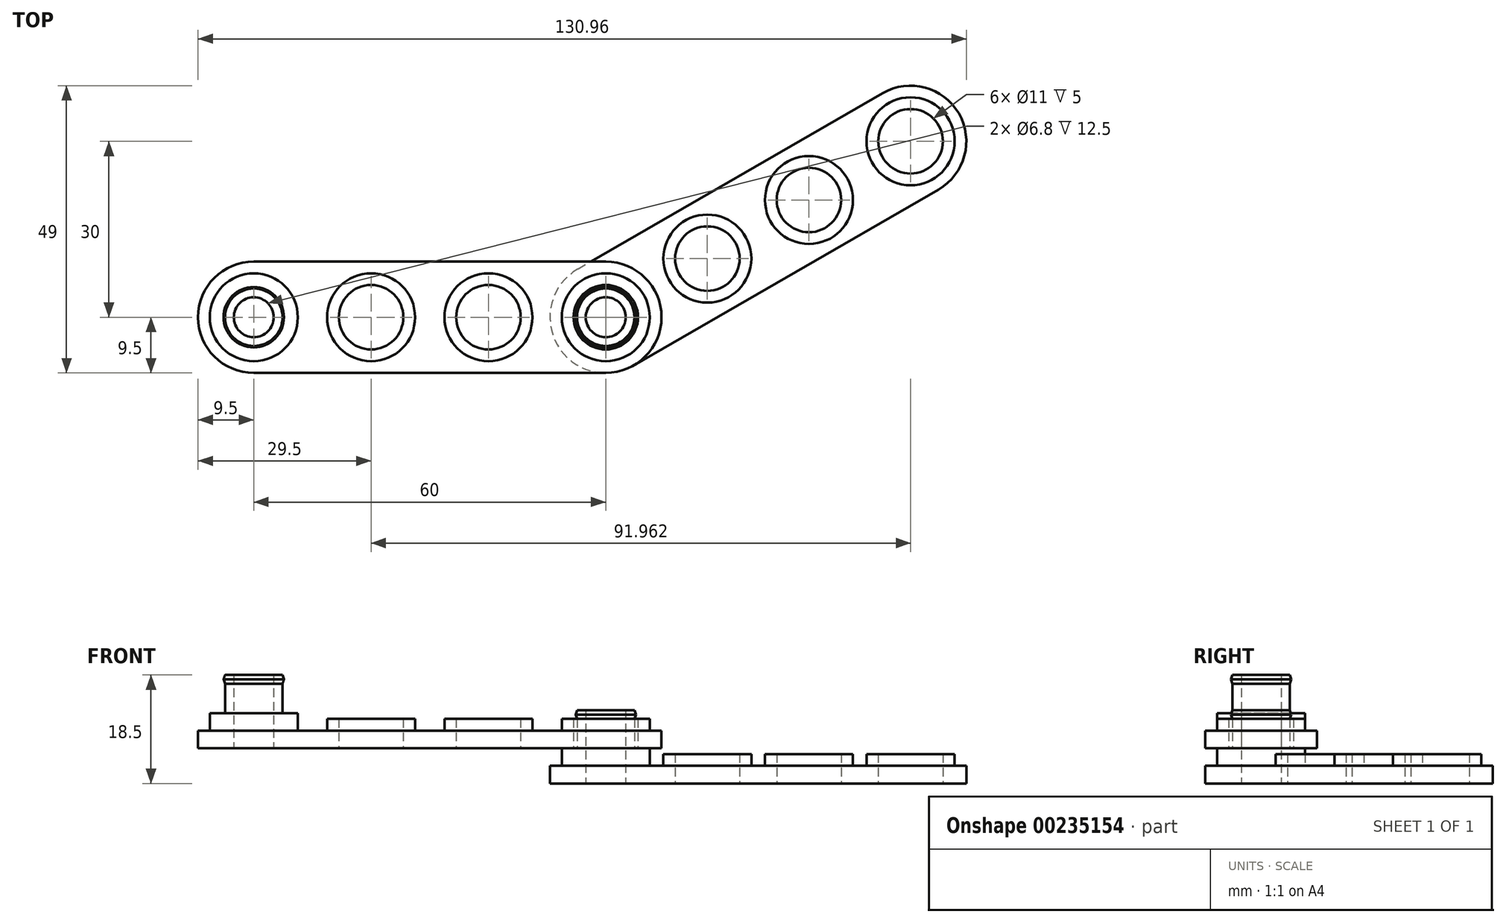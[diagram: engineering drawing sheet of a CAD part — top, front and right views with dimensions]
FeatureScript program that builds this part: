
annotation { "Feature Type Name" : "Feature", "Feature Type Description" : "" }
export const myFeature = defineFeature(function(context is Context, id is Id, definition is map)
    precondition{}
    {
        {
            var Q0;
            Q0=qCreatedBy(makeId("Top.planeOp"),FACE);
            var sketch = newSketch(context, id + "F0", { "sketchPlane" : qUnion([Q0])});
            skCircle(sketch, "E0", {"center": v(0, 0) * mm, "radius": 9.5 * mm});
            skLineSegment(sketch, "E1.bottom", {"start": v(0, 9.5) * mm, "end": v(60, 9.5) * mm});
            skLineSegment(sketch, "E1.top", {"start": v(0, -9.5) * mm, "end": v(60, -9.5) * mm});
            skCircle(sketch, "E2", {"center": v(60, 0) * mm, "radius": 9.5 * mm});
            skCircle(sketch, "E3", {"center": v(20, 0) * mm, "radius": 7.5 * mm});
            skCircle(sketch, "E4", {"center": v(0, 0) * mm, "radius": 7.5 * mm});
            skCircle(sketch, "E5", {"center": v(40, 0) * mm, "radius": 7.5 * mm});
            skCircle(sketch, "E6", {"center": v(60, 0) * mm, "radius": 7.5 * mm});
            skCircle(sketch, "E7", {"center": v(20, 0) * mm, "radius": 5.5 * mm});
            skCircle(sketch, "E8", {"center": v(40, 0) * mm, "radius": 5.5 * mm});
            skCircle(sketch, "E9", {"center": v(60, 0) * mm, "radius": 5.5 * mm});
            skCircle(sketch, "E10", {"center": v(0, 0) * mm, "radius": 4.9 * mm});
            skCircle(sketch, "E11", {"center": v(0, 0) * mm, "radius": 3.4 * mm});
            skSolve(sketch);
        }
        {
            var Q0;
            Q0 = qSketchRegion(id + "F0", true);
            extrude(context, id + "F1", {"entities" : qUnion([Q0]), "depth" : 3 * mm});
        }
        {
            var Q0;
            Q0=makeQuery(id+"F0.imprint","IMPRINT",FACE,{"disambiguationData":[TD([[makeQuery(id+"F0.imprint","IMPRINT",EDGE,{"derivedFrom":sQuery(id+"F0.wireOp",EDGE,"E3")}),1.0]])]});
            var Q1;
            Q1=makeQuery(id+"F0.imprint","IMPRINT",FACE,{"disambiguationData":[TD([[makeQuery(id+"F0.imprint","IMPRINT",EDGE,{"derivedFrom":sQuery(id+"F0.wireOp",EDGE,"E5")}),1.0]])]});
            var Q2;
            Q2=makeQuery(id+"F0.imprint","IMPRINT",FACE,{"disambiguationData":[TD([[makeQuery(id+"F0.imprint","IMPRINT",EDGE,{"derivedFrom":sQuery(id+"F0.wireOp",EDGE,"E6")}),1.0]])]});
            extrude(context, id + "F2", {"entities" : qUnion([Q0, Q1, Q2]), "operationType" : NewBodyOperationType.ADD, "depth" : 5 * mm});
        }
        {
            var Q0;
            Q0=makeQuery(id+"F0.imprint","IMPRINT",FACE,{"disambiguationData":[TD([[makeQuery(id+"F0.imprint","IMPRINT",EDGE,{"derivedFrom":sQuery(id+"F0.wireOp",EDGE,"E4")}),1.0]])]});
            extrude(context, id + "F3", {"entities" : qUnion([Q0]), "operationType" : NewBodyOperationType.ADD, "depth" : 6 * mm});
        }
        {
            var Q0;
            Q0=makeQuery(id+"F0.imprint","IMPRINT",FACE,{"disambiguationData":[TD([[makeQuery(id+"F0.imprint","IMPRINT",EDGE,{"derivedFrom":sQuery(id+"F0.wireOp",EDGE,"E10")}),1.0]])]});
            extrude(context, id + "F4", {"entities" : qUnion([Q0]), "operationType" : NewBodyOperationType.ADD, "depth" : 12.5 * mm});
        }
        {
            var Q0;
            Q0=qCreatedBy(makeId("Front.planeOp"),FACE);
            var sketch = newSketch(context, id + "F5", { "sketchPlane" : qUnion([Q0])});
            skLineSegment(sketch, "E12.bottom", {"start": v(0, 0) * mm, "end": v(4.9, 0) * mm});
            skLineSegment(sketch, "E12.top", {"start": v(0, 12.5) * mm, "end": v(4.9, 12.5) * mm});
            skLineSegment(sketch, "E12.left", {"start": v(0, 0) * mm, "end": v(0, 12.5) * mm});
            skLineSegment(sketch, "E12.right", {"start": v(4.9, 0) * mm, "end": v(4.9, 12.5) * mm});
            skLineSegment(sketch, "E13", {"start": v(4.9, 12.5) * mm, "end": v(5.15, 11.75) * mm});
            skLineSegment(sketch, "E14", {"start": v(5.15, 11.75) * mm, "end": v(4.9, 11) * mm});
            skSolve(sketch);
        }
        {
            var Q0;
            {var subQ0=sQuery(id+"F5.wireOp",EDGE,"E13");Q0=makeQuery(id+"F5.imprint","IMPRINT",FACE,{"disambiguationData":[TD([[makeQuery(id+"F5.imprint","IMPRINT",EDGE,{"derivedFrom":subQ0}),-1.0]])]});}
            var Q1;
            Q1=sQuery(id+"F5.wireOp",EDGE,"E12.left");
            revolve(context, id + "F6", {"operationType" : NewBodyOperationType.ADD, "entities" : qUnion([Q0]), "axis" : qUnion([Q1]), "revolveType" : RevolveType.FULL});
        }
        {
            var Q0;
            Q0=makeQuery(id+"F1.opExtrude","SWEPT_BODY",BODY,{"disambiguationData":[OSD([sQuery(id+"F0.wireOp",EDGE,"E0"),sQuery(id+"F0.wireOp",EDGE,"E1.bottom"),sQuery(id+"F0.wireOp",EDGE,"E1.top"),sQuery(id+"F0.wireOp",EDGE,"E2"),sQuery(id+"F0.wireOp",EDGE,"E3"),sQuery(id+"F0.wireOp",EDGE,"E4"),sQuery(id+"F0.wireOp",EDGE,"E5"),sQuery(id+"F0.wireOp",EDGE,"E6")])]});
            transform(context, id + "F7", {"entities" : qUnion([Q0]), "transformType" : TransformType.TRANSLATION_3D, "dx" : 60 * mm, "dy" : 0 * mm, "dz" : -6 * mm, "makeCopy" : true});
        }
        {
            var Q0;
            Q0=makeQuery(id+"F7.opPattern","COPY",BODY,{"derivedFrom":makeQuery(id+"F1.opExtrude","SWEPT_BODY",BODY,{"disambiguationData":[OSD([sQuery(id+"F0.wireOp",EDGE,"E0"),sQuery(id+"F0.wireOp",EDGE,"E1.bottom"),sQuery(id+"F0.wireOp",EDGE,"E1.top"),sQuery(id+"F0.wireOp",EDGE,"E2"),sQuery(id+"F0.wireOp",EDGE,"E3"),sQuery(id+"F0.wireOp",EDGE,"E4"),sQuery(id+"F0.wireOp",EDGE,"E5"),sQuery(id+"F0.wireOp",EDGE,"E6")])]}),"instanceName":"1"});
            var Q1;
            Q1=makeQuery(id+"F7.opPattern","COPY",EDGE,{"derivedFrom":makeQuery(id+"F6.boolean.opBoolean","MERGE",EDGE,{"derivedFrom":[makeQuery(id+"F4.opExtrude","CAP_EDGE",EDGE,{"disambiguationData":[OSD([sQuery(id+"F0.wireOp",EDGE,"E10")])],"isStart":false}),makeQuery(id+"F6.opRevolve","SWEPT_EDGE",EDGE,{"disambiguationData":[OSD([sQuery(id+"F5.wireOp",EDGE,"E12.top"),sQuery(id+"F5.wireOp",EDGE,"E12.right"),sQuery(id+"F5.wireOp",EDGE,"E13")])]})]}),"instanceName":"1"});
            transform(context, id + "F8", {"entities" : qUnion([Q0]), "transformType" : TransformType.ROTATION, "transformAxis" : qUnion([Q1]), "angle" : 30 * degree, "oppositeDirection" : true, "makeCopy" : false});
        }
    });
